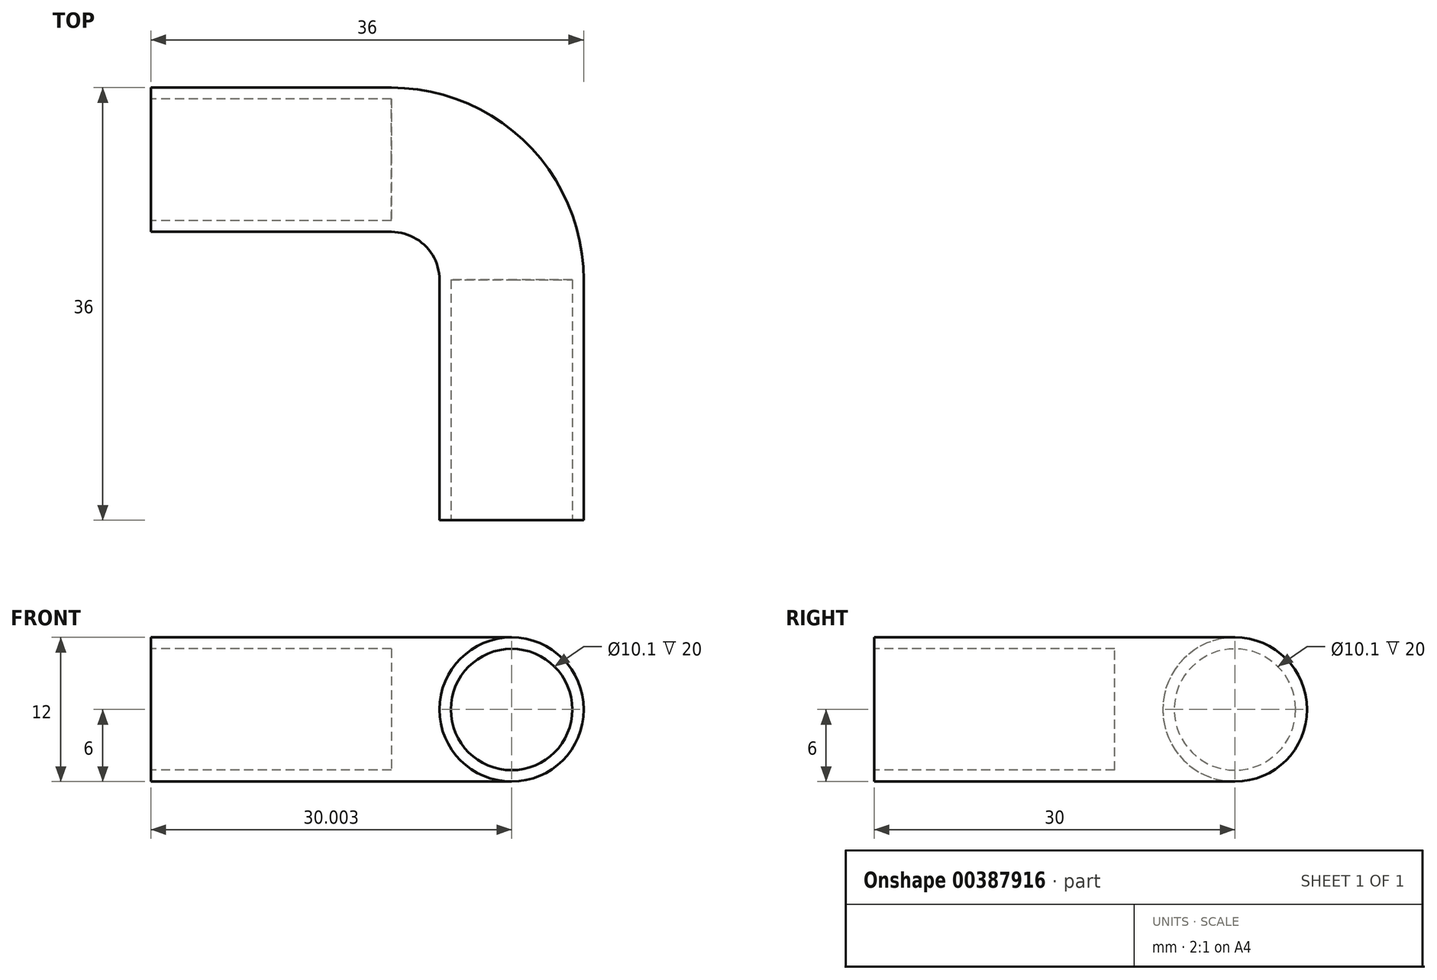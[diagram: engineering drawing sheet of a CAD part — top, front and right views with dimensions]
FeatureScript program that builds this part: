
annotation { "Feature Type Name" : "Feature", "Feature Type Description" : "" }
export const myFeature = defineFeature(function(context is Context, id is Id, definition is map)
    precondition{}
    {
        {
            var Q0;
            Q0=qCreatedBy(makeId("Top.planeOp"),FACE);
            var sketch = newSketch(context, id + "F0", { "sketchPlane" : qUnion([Q0])});
            skLineSegment(sketch, "E0", {"start": v(-8.65, 0) * mm, "end": v(-8.65, 20) * mm});
            skLineSegment(sketch, "E1", {"start": v(-18.65, 30) * mm, "end": v(-38.65, 30) * mm});
            skArc(sketch, "E2.filletArc", {"start": v(-8.65, 20) * mm, "mid": v(-11.58, 27.07) * mm, "end": v(-18.65, 30) * mm});
            skSolve(sketch);
        }
        {
            var Q0;
            Q0=qCreatedBy(makeId("Front.planeOp"),FACE);
            var sketch = newSketch(context, id + "F1", { "sketchPlane" : qUnion([Q0])});
            skCircle(sketch, "E3", {"center": v(-8.65, 0) * mm, "radius": 6 * mm});
            skSolve(sketch);
        }
        {
            var Q0;
            Q0=makeQuery(id+"F1.imprint","IMPRINT",FACE,{"disambiguationData":[TD([[makeQuery(id+"F1.imprint","IMPRINT",EDGE,{"derivedFrom":sQuery(id+"F1.wireOp",EDGE,"E3")}),1.0]])]});
            var sketch = newSketch(context, id + "F2", { "sketchPlane" : qUnion([Q0])});
            skSolve(sketch);
        }
        {
            var Q0;
            Q0=makeQuery(id+"F1.imprint","IMPRINT",FACE,{"disambiguationData":[TD([[makeQuery(id+"F1.imprint","IMPRINT",EDGE,{"derivedFrom":sQuery(id+"F1.wireOp",EDGE,"E3")}),1.0]])]});
            var Q1;
            Q1=sQuery(id+"F0.wireOp",EDGE,"E0");
            var Q2;
            Q2=sQuery(id+"F0.wireOp",EDGE,"E2.filletArc");
            var Q3;
            Q3=sQuery(id+"F0.wireOp",EDGE,"E1");
            sweep(context, id + "F3", {"profiles" : qUnion([Q0]), "path" : qUnion([Q1, Q2, Q3])});
        }
        {
            var Q0;
            Q0=makeQuery(id+"F2.imprint","IMPRINT",FACE,{"disambiguationData":[TD([[makeQuery(id+"F2.imprint","IMPRINT",EDGE,{"derivedFrom":makeQuery(id+"F1.imprint","IMPRINT",EDGE,{"derivedFrom":sQuery(id+"F1.wireOp",EDGE,"E3")})}),1.0]])]});
            var sketch = newSketch(context, id + "F4", { "sketchPlane" : qUnion([Q0])});
            skCircle(sketch, "E4", {"center": v(-8.65, 0) * mm, "radius": 5.05 * mm});
            skSolve(sketch);
        }
        {
            var Q0;
            Q0=makeQuery(id+"F4.imprint","IMPRINT",FACE,{"disambiguationData":[TD([[makeQuery(id+"F4.imprint","IMPRINT",EDGE,{"derivedFrom":sQuery(id+"F4.wireOp",EDGE,"E4")}),1.0]])]});
            extrude(context, id + "F5", {"entities" : qUnion([Q0]), "operationType" : NewBodyOperationType.REMOVE, "oppositeDirection" : true, "depth" : 20 * mm});
        }
        {
            var Q0;
            Q0=makeQuery(id+"F3.opSweep","CAP_FACE",FACE,{"disambiguationData":[OSD([sQuery(id+"F0.wireOp",VERTEX,"E1.end"),sQuery(id+"F1.wireOp",EDGE,"E3")])],"isStart":false});
            var sketch = newSketch(context, id + "F6", { "sketchPlane" : qUnion([Q0])});
            skCircle(sketch, "E5", {"center": v(-30, 0) * mm, "radius": 5.05 * mm});
            skSolve(sketch);
        }
        {
            var Q0;
            Q0=makeQuery(id+"F6.imprint","IMPRINT",FACE,{"disambiguationData":[TD([[makeQuery(id+"F6.imprint","IMPRINT",EDGE,{"derivedFrom":sQuery(id+"F6.wireOp",EDGE,"E5")}),1.0]])]});
            extrude(context, id + "F7", {"entities" : qUnion([Q0]), "operationType" : NewBodyOperationType.REMOVE, "oppositeDirection" : true, "depth" : 20 * mm});
        }
    });
